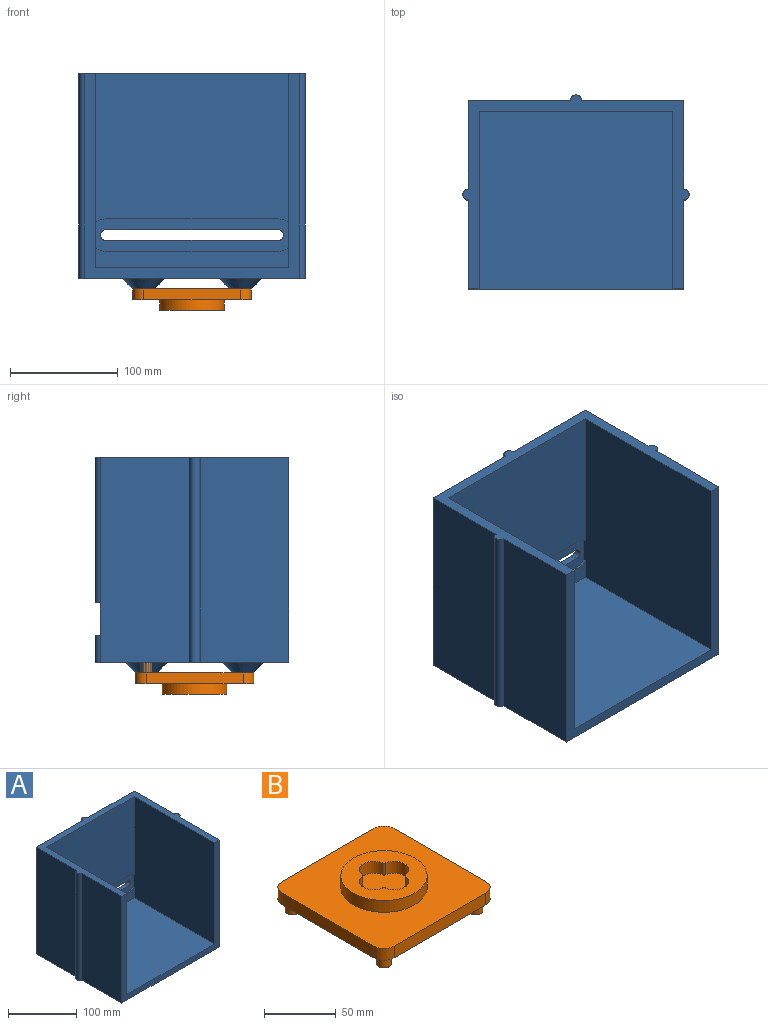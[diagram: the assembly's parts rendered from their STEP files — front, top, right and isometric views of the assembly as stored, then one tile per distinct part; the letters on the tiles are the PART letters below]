
ASSEMBLY  parts=2 mates=1
PART A: 54 faces, bbox 210x180x200 mm
  f0: plane 190x82.5mm, normal (-1,0,0), area 15675mm2, adj f19,f21,f33,f53
  f1: plane 190x82.5mm, normal (1,0,0), area 15675mm2, adj f19,f21,f33,f52
  f2: plane 190x94.96mm, normal (0,1,0), area 15516.9mm2, adj f10,f11,f19,f20,f21,f26,f27,f28
  f3: plane 190x94.96mm, normal (0,1,0), area 15516.9mm2, adj f9,f18,f19,f21,f25,f26,f27,f29
  f4: plane 180x138.82mm, normal (0,-1,0), area 24324mm2, adj f5,f7,f21,f22,f30,f32
  f5: cylinder r=15mm len=10mm, axis (0,-1,0), area 21.9mm2, adj f4,f8,f22,f32
  f6: cylinder r=15mm len=10mm, axis (0,-1,0), area 21.9mm2, adj f8,f17,f24,f32
  f7: cylinder r=15mm len=10mm, axis (0,-1,0), area 21.9mm2, adj f4,f8,f22,f30
  f8: plane 180x30mm, normal (0,-1,0), area 3673.4mm2, adj f5,f6,f7,f13,f14,f15,f16,f22
  f9: cylinder r=15mm len=10mm, axis (0,1,0), area 21.9mm2, adj f3,f12,f27,f29
  f10: cylinder r=15mm len=10mm, axis (0,1,0), area 21.9mm2, adj f2,f12,f27,f28
  f11: cylinder r=15mm len=10mm, axis (0,1,0), area 21.9mm2, adj f2,f12,f26,f28
  f12: plane 180x30mm, normal (0,1,0), area 3673.4mm2, adj f9,f10,f11,f13,f14,f15,f16,f25
  f13: plane 160x6mm, normal (0,0,-1), area 960mm2, adj f8,f12,f14,f16
  f14: cylinder r=5mm len=10mm, axis (0,1,0), area 94.2mm2, adj f8,f12,f13,f15
  f15: plane 160x6mm, normal (0,0,1), area 960mm2, adj f8,f12,f14,f16
  f16: cylinder r=5mm len=10mm, axis (0,1,0), area 94.2mm2, adj f8,f12,f13,f15
  f17: plane 180x18.82mm, normal (0,-1,0), area 2724mm2, adj f6,f23,f24,f30,f31,f32
  f18: plane 190x82.5mm, normal (-1,0,0), area 15675mm2, adj f3,f19,f21,f53
  f19: plane 210x180.04mm, normal (0,0,-1), area 30092mm2, adj f0,f1,f2,f3,f18,f20,f33,f36
  f20: plane 190x82.5mm, normal (1,0,0), area 15675mm2, adj f2,f19,f21,f52
  f21: plane 210x180.04mm, normal (0,0,1), area 5418.5mm2, adj f0,f1,f2,f3,f4,f18,f20,f30
  f22: plane 160x2mm, normal (0,0,-1), area 320mm2, adj f4,f5,f7,f8
  f23: cylinder r=15mm len=10mm, axis (0,-1,0), area 21.9mm2, adj f8,f17,f24,f30
  f24: plane 160x2mm, normal (0,0,1), area 320mm2, adj f6,f8,f17,f23
  f25: cylinder r=15mm len=10mm, axis (0,1,0), area 21.9mm2, adj f3,f12,f26,f29
  f26: plane 160x7.04mm, normal (0,0,-1), area 360mm2, adj f2,f3,f11,f12,f25,f50
  f27: plane 160x7.04mm, normal (0,0,1), area 360mm2, adj f2,f3,f9,f10,f12,f51
  f28: plane 22.36x2mm, normal (-1,0,0), area 44.7mm2, adj f2,f10,f11,f12
  f29: plane 22.36x2mm, normal (1,0,0), area 44.7mm2, adj f3,f9,f12,f25
  f30: plane 180x167mm, normal (1,0,0), area 29744.7mm2, adj f4,f7,f8,f17,f21,f23,f31,f33
  f31: plane 180x165mm, normal (0,0,1), area 29700mm2, adj f17,f30,f32,f33
  f32: plane 180x167mm, normal (-1,0,0), area 29744.7mm2, adj f4,f5,f6,f8,f17,f21,f31,f33
  f33: plane 200x190mm, normal (0,-1,0), area 5600mm2, adj f0,f1,f19,f21,f30,f31,f32
  f34: cylinder r=5mm len=10mm, axis (0,0,-1), area 314.2mm2, adj f35,f37
  f35: plane 20x20mm, normal (0,0,-1), area 235.6mm2, adj f34,f36
  f36: cone r=20mm half-angle=45deg, axis (0,0,1), area 1332.9mm2, adj f19,f35
  f37: plane 10x10mm, normal (0,0,-1), area 78.5mm2, adj f34
  f38: cylinder r=5mm len=10mm, axis (0,0,-1), area 314.2mm2, adj f39,f41
  f39: plane 20x20mm, normal (0,0,-1), area 235.6mm2, adj f38,f40
  f40: cone r=20mm half-angle=45deg, axis (0,0,1), area 1332.9mm2, adj f19,f39
  f41: plane 10x10mm, normal (0,0,-1), area 78.5mm2, adj f38
  f42: cylinder r=5mm len=10mm, axis (0,0,-1), area 314.2mm2, adj f43,f45
  f43: plane 20x20mm, normal (0,0,-1), area 235.6mm2, adj f42,f44
  f44: cone r=20mm half-angle=45deg, axis (0,0,1), area 1332.9mm2, adj f19,f43
  f45: plane 10x10mm, normal (0,0,-1), area 78.5mm2, adj f42
  f46: cylinder r=5mm len=10mm, axis (0,0,-1), area 314.2mm2, adj f47,f49
  f47: plane 20x20mm, normal (0,0,-1), area 235.6mm2, adj f46,f48
  f48: cone r=20mm half-angle=45deg, axis (0,0,1), area 1332.9mm2, adj f19,f47
  f49: plane 10x10mm, normal (0,0,-1), area 78.5mm2, adj f46
  f50: cylinder r=5.04mm len=135mm, axis (0,0,1), area 2139.5mm2, adj f2,f3,f21,f26
  f51: cylinder r=5.04mm len=25mm, axis (0,0,-1), area 396.2mm2, adj f2,f3,f19,f27
  f52: cylinder r=5mm len=190mm, axis (0,0,-1), area 2984.5mm2, adj f1,f19,f20,f21
  f53: cylinder r=5mm len=190mm, axis (0,0,-1), area 2984.5mm2, adj f0,f18,f19,f21
PART B: 29 faces, bbox 110x110x30 mm
  f0: plane 90x10mm, normal (0,-1,0), area 900mm2, adj f1,f7,f8,f9
  f1: cylinder r=10mm len=10mm, axis (0,0,-1), area 157.1mm2, adj f0,f2,f8,f9
  f2: plane 90x10mm, normal (1,0,0), area 900mm2, adj f1,f3,f8,f9
  f3: cylinder r=10mm len=10mm, axis (0,0,-1), area 157.1mm2, adj f2,f4,f8,f9
  f4: plane 90x10mm, normal (0,1,0), area 900mm2, adj f3,f5,f8,f9
  f5: cylinder r=10mm len=10mm, axis (0,0,-1), area 157.1mm2, adj f4,f6,f8,f9
  f6: plane 90x10mm, normal (-1,0,0), area 900mm2, adj f5,f7,f8,f9
  f7: cylinder r=10mm len=10mm, axis (0,0,-1), area 157.1mm2, adj f0,f6,f8,f9
  f8: plane 110x110mm, normal (0,0,1), area 9186.8mm2, adj f0,f1,f2,f3,f4,f5,f6,f7
  f9: plane 110x110mm, normal (0,0,-1), area 11700.1mm2, adj f0,f1,f2,f3,f4,f5,f6,f7
  f10: cylinder r=5mm len=10mm, axis (0,0,1), area 314.2mm2, adj f9,f11
  f11: plane 10x10mm, normal (0,0,-1), area 78.5mm2, adj f10
  f12: cylinder r=5mm len=10mm, axis (0,0,1), area 314.2mm2, adj f9,f13
  f13: plane 10x10mm, normal (0,0,-1), area 78.5mm2, adj f12
  f14: cylinder r=5mm len=10mm, axis (0,0,1), area 314.2mm2, adj f9,f15
  f15: plane 10x10mm, normal (0,0,-1), area 78.5mm2, adj f14
  f16: cylinder r=5mm len=10mm, axis (0,0,1), area 314.2mm2, adj f9,f17
  f17: plane 10x10mm, normal (0,0,-1), area 78.5mm2, adj f16
  f18: cylinder r=10mm len=19.76mm, axis (0,0,-1), area 283.1mm2, adj f19,f25,f27,f28
  f19: cylinder r=2mm len=10mm, axis (0,0,-1), area 25.2mm2, adj f18,f20,f27,f28
  f20: cylinder r=10mm len=19.76mm, axis (0,0,-1), area 283.1mm2, adj f19,f21,f27,f28
  f21: cylinder r=2mm len=10mm, axis (0,0,-1), area 25.2mm2, adj f20,f22,f27,f28
  f22: cylinder r=10mm len=19.76mm, axis (0,0,-1), area 283.1mm2, adj f21,f23,f27,f28
  f23: cylinder r=2mm len=10mm, axis (0,0,-1), area 25.2mm2, adj f22,f24,f27,f28
  f24: cylinder r=10mm len=19.76mm, axis (0,0,-1), area 283.1mm2, adj f23,f25,f27,f28
  f25: cylinder r=2mm len=10mm, axis (0,0,-1), area 25.2mm2, adj f18,f24,f27,f28
  f26: cylinder r=30mm len=60mm, axis (0,0,-1), area 1885mm2, adj f8,f27
  f27: plane 60x60mm, normal (0,0,1), area 1797.1mm2, adj f18,f19,f20,f21,f22,f23,f24,f25
  f28: plane 40x40mm, normal (0,0,1), area 1030.4mm2, adj f18,f19,f20,f21,f22,f23,f24,f25
PLACE A t=(0.6,0,-0.18)mm
PLACE B rot(axis=(0.71,0.71,0),180deg) t=(3.6,-90.5,-50.18)mm
MATE fastened B.f7 <-> A.f48  axis (0,0,1) through (-44.4,-132.5,-40.18)mm
